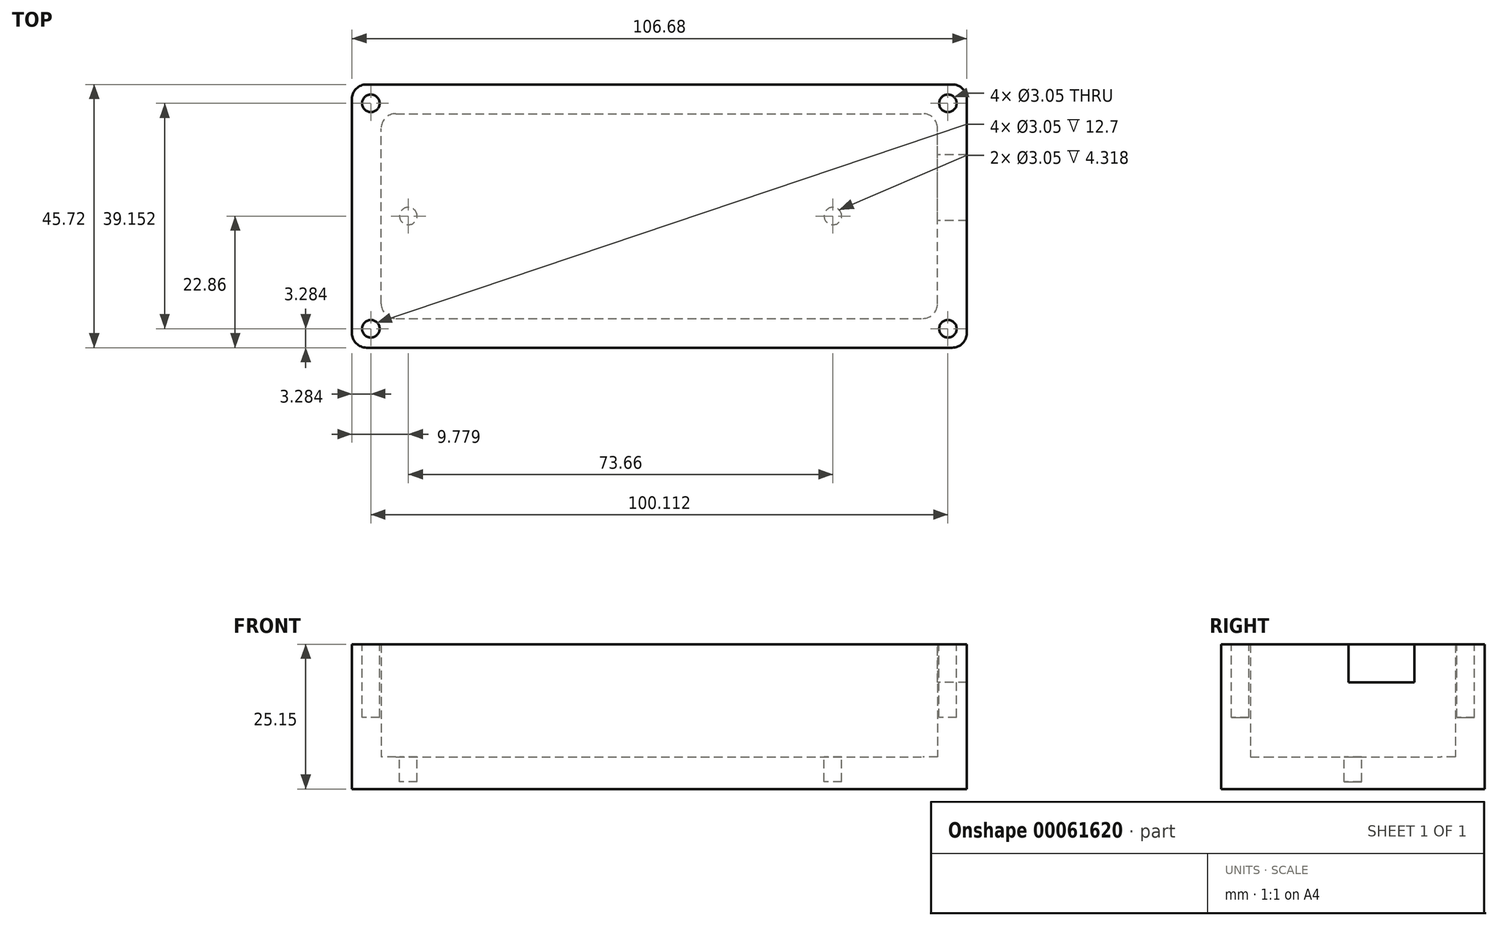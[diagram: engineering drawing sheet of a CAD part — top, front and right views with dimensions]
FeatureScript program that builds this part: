
annotation { "Feature Type Name" : "Feature", "Feature Type Description" : "" }
export const myFeature = defineFeature(function(context is Context, id is Id, definition is map)
    precondition{}
    {
        {
            var Q0;
            Q0=qCreatedBy(makeId("Top.planeOp"),FACE);
            var sketch = newSketch(context, id + "F0", { "sketchPlane" : qUnion([Q0])});
            skLineSegment(sketch, "E0.bottom", {"start": v(2.54, 0) * mm, "end": v(93.98, 0) * mm});
            skLineSegment(sketch, "E0.top", {"start": v(2.54, 35.56) * mm, "end": v(93.98, 35.56) * mm});
            skLineSegment(sketch, "E0.left", {"start": v(0, 2.54) * mm, "end": v(0, 33.02) * mm});
            skLineSegment(sketch, "E0.right", {"start": v(96.52, 2.54) * mm, "end": v(96.52, 33.02) * mm});
            skLineSegment(sketch, "E1.0", {"start": v(-2.54, 40.64) * mm, "end": v(99.06, 40.64) * mm});
            skLineSegment(sketch, "E1.1", {"start": v(-5.08, -2.54) * mm, "end": v(-5.08, 38.1) * mm});
            skLineSegment(sketch, "E1.2", {"start": v(-2.54, -5.08) * mm, "end": v(99.06, -5.08) * mm});
            skLineSegment(sketch, "E1.3", {"start": v(101.6, -2.54) * mm, "end": v(101.6, 38.1) * mm});
            skPoint(sketch, "E2.visualSharp", {"position": v(-5.08, -5.08) * mm});
            skArc(sketch, "E2.filletArc", {"start": v(-5.08, -2.54) * mm, "mid": v(-4.34, -4.34) * mm, "end": v(-2.54, -5.08) * mm});
            skPoint(sketch, "E3.visualSharp", {"position": v(101.6, 40.64) * mm});
            skArc(sketch, "E3.filletArc", {"start": v(101.6, 38.1) * mm, "mid": v(100.86, 39.9) * mm, "end": v(99.06, 40.64) * mm});
            skPoint(sketch, "E4.visualSharp", {"position": v(101.6, -5.08) * mm});
            skArc(sketch, "E4.filletArc", {"start": v(99.06, -5.08) * mm, "mid": v(100.86, -4.34) * mm, "end": v(101.6, -2.54) * mm});
            skPoint(sketch, "E5.visualSharp", {"position": v(-5.08, 40.64) * mm});
            skArc(sketch, "E5.filletArc", {"start": v(-2.54, 40.64) * mm, "mid": v(-4.34, 39.9) * mm, "end": v(-5.08, 38.1) * mm});
            skPoint(sketch, "E6.visualSharp", {"position": v(0, 0) * mm});
            skArc(sketch, "E6.filletArc", {"start": v(0, 2.54) * mm, "mid": v(0.74, 0.74) * mm, "end": v(2.54, 0) * mm});
            skPoint(sketch, "E7.visualSharp", {"position": v(0, 35.56) * mm});
            skArc(sketch, "E7.filletArc", {"start": v(2.54, 35.56) * mm, "mid": v(0.74, 34.82) * mm, "end": v(0, 33.02) * mm});
            skPoint(sketch, "E8.visualSharp", {"position": v(96.52, 35.56) * mm});
            skArc(sketch, "E8.filletArc", {"start": v(96.52, 33.02) * mm, "mid": v(95.78, 34.82) * mm, "end": v(93.98, 35.56) * mm});
            skPoint(sketch, "E9.visualSharp", {"position": v(96.52, 0) * mm});
            skArc(sketch, "E9.filletArc", {"start": v(93.98, 0) * mm, "mid": v(95.78, 0.74) * mm, "end": v(96.52, 2.54) * mm});
            skLineSegment(sketch, "E10.bottom", {"start": v(0.89, 1.27) * mm, "end": v(82.17, 1.27) * mm, "construction": true});
            skLineSegment(sketch, "E10.top", {"start": v(0.89, 34.3) * mm, "end": v(82.17, 34.3) * mm, "construction": true});
            skLineSegment(sketch, "E10.left", {"start": v(0.89, 1.27) * mm, "end": v(0.89, 34.3) * mm, "construction": true});
            skLineSegment(sketch, "E10.right", {"start": v(82.17, 1.27) * mm, "end": v(82.17, 34.3) * mm, "construction": true});
            skPoint(sketch, "E11", {"position": v(0, 17.78) * mm});
            skPoint(sketch, "E12", {"position": v(0.89, 17.78) * mm});
            skCircle(sketch, "E13", {"center": v(4.7, 17.78) * mm, "radius": 1.52 * mm});
            skCircle(sketch, "E14", {"center": v(78.36, 17.78) * mm, "radius": 1.52 * mm});
            skLineSegment(sketch, "E15", {"start": v(4.7, 17.78) * mm, "end": v(78.36, 17.78) * mm, "construction": true});
            skPoint(sketch, "E16", {"position": v(41.53, 17.78) * mm});
            skPoint(sketch, "E17", {"position": v(41.53, 34.3) * mm});
            skLineSegment(sketch, "E18.bottom", {"start": v(40.26, 31.12) * mm, "end": v(95.63, 31.12) * mm, "construction": true});
            skLineSegment(sketch, "E18.top", {"start": v(40.26, 4.44) * mm, "end": v(95.63, 4.44) * mm, "construction": true});
            skLineSegment(sketch, "E18.left", {"start": v(40.26, 31.12) * mm, "end": v(40.26, 4.44) * mm, "construction": true});
            skLineSegment(sketch, "E18.right", {"start": v(95.63, 31.12) * mm, "end": v(95.63, 4.44) * mm, "construction": true});
            skPoint(sketch, "E19", {"position": v(95.63, 17.78) * mm});
            skLineSegment(sketch, "E20", {"start": v(0, 17.78) * mm, "end": v(0.89, 17.78) * mm, "construction": true});
            skLineSegment(sketch, "E21", {"start": v(95.63, 17.78) * mm, "end": v(96.52, 17.78) * mm, "construction": true});
            skLineSegment(sketch, "E22.bottom", {"start": v(95.63, 27.3) * mm, "end": v(90.55, 27.3) * mm, "construction": true});
            skLineSegment(sketch, "E22.top", {"start": v(95.63, 18.16) * mm, "end": v(90.55, 18.16) * mm, "construction": true});
            skLineSegment(sketch, "E22.left", {"start": v(95.63, 27.3) * mm, "end": v(95.63, 18.16) * mm, "construction": true});
            skLineSegment(sketch, "E22.right", {"start": v(90.55, 27.3) * mm, "end": v(90.55, 18.16) * mm, "construction": true});
            skPoint(sketch, "E23", {"position": v(90.55, 22.73) * mm});
            skSolve(sketch);
        }
        {
            var Q0;
            Q0 = qSketchRegion(id + "F0", true);
            extrude(context, id + "F1", {"entities" : qUnion([Q0]), "depth" : 19.56 * mm});
        }
        {
            var Q0;
            Q0=makeQuery(id+"F0.imprint","IMPRINT",FACE,{"disambiguationData":[TD([[makeQuery(id+"F0.imprint","IMPRINT",EDGE,{"derivedFrom":sQuery(id+"F0.wireOp",EDGE,"E0.bottom")}),-1.0]])]});
            var Q1;
            Q1=makeQuery(id+"F0.imprint","IMPRINT",FACE,{"disambiguationData":[TD([[makeQuery(id+"F0.imprint","IMPRINT",EDGE,{"derivedFrom":sQuery(id+"F0.wireOp",EDGE,"E0.bottom")}),1.0]])]});
            var Q2;
            Q2=makeQuery(id+"F0.imprint","IMPRINT",FACE,{"disambiguationData":[TD([[makeQuery(id+"F0.imprint","IMPRINT",EDGE,{"derivedFrom":sQuery(id+"F0.wireOp",EDGE,"E14")}),1.0]])]});
            var Q3;
            Q3=makeQuery(id+"F0.imprint","IMPRINT",FACE,{"disambiguationData":[TD([[makeQuery(id+"F0.imprint","IMPRINT",EDGE,{"derivedFrom":sQuery(id+"F0.wireOp",EDGE,"E13")}),1.0]])]});
            extrude(context, id + "F2", {"entities" : qUnion([Q0, Q1, Q2, Q3]), "operationType" : NewBodyOperationType.ADD, "oppositeDirection" : true, "depth" : 5.6 * mm});
        }
        {
            var Q0;
            Q0=makeQuery(id+"F1.opExtrude","CAP_FACE",FACE,{"disambiguationData":[OSD([sQuery(id+"F0.wireOp",EDGE,"E0.bottom"),sQuery(id+"F0.wireOp",EDGE,"E0.top"),sQuery(id+"F0.wireOp",EDGE,"E0.left"),sQuery(id+"F0.wireOp",EDGE,"E0.right"),sQuery(id+"F0.wireOp",EDGE,"E1.0"),sQuery(id+"F0.wireOp",EDGE,"E1.1"),sQuery(id+"F0.wireOp",EDGE,"E1.2"),sQuery(id+"F0.wireOp",EDGE,"E1.3"),sQuery(id+"F0.wireOp",EDGE,"E2.filletArc"),sQuery(id+"F0.wireOp",EDGE,"E3.filletArc"),sQuery(id+"F0.wireOp",EDGE,"E4.filletArc"),sQuery(id+"F0.wireOp",EDGE,"E5.filletArc"),sQuery(id+"F0.wireOp",EDGE,"E6.filletArc"),sQuery(id+"F0.wireOp",EDGE,"E7.filletArc"),sQuery(id+"F0.wireOp",EDGE,"E8.filletArc"),sQuery(id+"F0.wireOp",EDGE,"E9.filletArc")])],"isStart":false});
            var sketch = newSketch(context, id + "F3", { "sketchPlane" : qUnion([Q0])});
            skLineSegment(sketch, "E24", {"start": v(0.74, 0.74) * mm, "end": v(-4.34, -4.34) * mm, "construction": true});
            skCircle(sketch, "E25", {"center": v(-1.8, -1.8) * mm, "radius": 1.52 * mm});
            skLineSegment(sketch, "E26", {"start": v(-4.34, 39.9) * mm, "end": v(0.74, 34.82) * mm, "construction": true});
            skLineSegment(sketch, "E27", {"start": v(95.78, 34.82) * mm, "end": v(100.86, 39.9) * mm, "construction": true});
            skLineSegment(sketch, "E28", {"start": v(95.78, 0.74) * mm, "end": v(100.86, -4.34) * mm, "construction": true});
            skCircle(sketch, "E29", {"center": v(-1.8, 37.36) * mm, "radius": 1.52 * mm});
            skCircle(sketch, "E30", {"center": v(98.32, 37.36) * mm, "radius": 1.52 * mm});
            skCircle(sketch, "E31", {"center": v(98.32, -1.8) * mm, "radius": 1.52 * mm});
            skSolve(sketch);
        }
        {
            var Q0;
            Q0 = qSketchRegion(id + "F3", true);
            extrude(context, id + "F4", {"entities" : qUnion([Q0]), "operationType" : NewBodyOperationType.REMOVE, "oppositeDirection" : true, "depth" : 12.7 * mm});
        }
        {
            var Q0;
            Q0=makeQuery(id+"F1.opExtrude","CAP_FACE",FACE,{"disambiguationData":[OSD([sQuery(id+"F0.wireOp",EDGE,"E0.bottom"),sQuery(id+"F0.wireOp",EDGE,"E0.top"),sQuery(id+"F0.wireOp",EDGE,"E0.left"),sQuery(id+"F0.wireOp",EDGE,"E0.right"),sQuery(id+"F0.wireOp",EDGE,"E1.0"),sQuery(id+"F0.wireOp",EDGE,"E1.1"),sQuery(id+"F0.wireOp",EDGE,"E1.2"),sQuery(id+"F0.wireOp",EDGE,"E1.3"),sQuery(id+"F0.wireOp",EDGE,"E2.filletArc"),sQuery(id+"F0.wireOp",EDGE,"E3.filletArc"),sQuery(id+"F0.wireOp",EDGE,"E4.filletArc"),sQuery(id+"F0.wireOp",EDGE,"E5.filletArc"),sQuery(id+"F0.wireOp",EDGE,"E6.filletArc"),sQuery(id+"F0.wireOp",EDGE,"E7.filletArc"),sQuery(id+"F0.wireOp",EDGE,"E8.filletArc"),sQuery(id+"F0.wireOp",EDGE,"E9.filletArc")])],"isStart":false});
            var sketch = newSketch(context, id + "F5", { "sketchPlane" : qUnion([Q0])});
            skLineSegment(sketch, "E32.bottom", {"start": v(101.6, 28.45) * mm, "end": v(96.52, 28.45) * mm});
            skLineSegment(sketch, "E32.top", {"start": v(101.6, 17.02) * mm, "end": v(96.52, 17.02) * mm});
            skLineSegment(sketch, "E32.left", {"start": v(101.6, 28.45) * mm, "end": v(101.6, 17.02) * mm});
            skLineSegment(sketch, "E32.right", {"start": v(96.52, 28.45) * mm, "end": v(96.52, 17.02) * mm});
            skPoint(sketch, "E33", {"position": v(96.52, 22.73) * mm});
            skSolve(sketch);
        }
        {
            var Q0;
            Q0 = qSketchRegion(id + "F5", true);
            extrude(context, id + "F6", {"entities" : qUnion([Q0]), "operationType" : NewBodyOperationType.REMOVE, "oppositeDirection" : true, "depth" : 6.6 * mm});
        }
        {
            var Q0;
            Q0=makeQuery(id+"F0.imprint","IMPRINT",FACE,{"disambiguationData":[TD([[makeQuery(id+"F0.imprint","IMPRINT",EDGE,{"derivedFrom":sQuery(id+"F0.wireOp",EDGE,"E13")}),1.0]])]});
            var Q1;
            Q1=makeQuery(id+"F0.imprint","IMPRINT",FACE,{"disambiguationData":[TD([[makeQuery(id+"F0.imprint","IMPRINT",EDGE,{"derivedFrom":sQuery(id+"F0.wireOp",EDGE,"E14")}),1.0]])]});
            extrude(context, id + "F7", {"entities" : qUnion([Q0, Q1]), "operationType" : NewBodyOperationType.REMOVE, "oppositeDirection" : true, "depth" : 4.32 * mm});
        }
        {
            var Q0;
            Q0=makeQuery(id+"F1.opExtrude","CAP_FACE",FACE,{"disambiguationData":[OSD([sQuery(id+"F0.wireOp",EDGE,"E0.bottom"),sQuery(id+"F0.wireOp",EDGE,"E0.top"),sQuery(id+"F0.wireOp",EDGE,"E0.left"),sQuery(id+"F0.wireOp",EDGE,"E0.right"),sQuery(id+"F0.wireOp",EDGE,"E1.0"),sQuery(id+"F0.wireOp",EDGE,"E1.1"),sQuery(id+"F0.wireOp",EDGE,"E1.2"),sQuery(id+"F0.wireOp",EDGE,"E1.3"),sQuery(id+"F0.wireOp",EDGE,"E2.filletArc"),sQuery(id+"F0.wireOp",EDGE,"E3.filletArc"),sQuery(id+"F0.wireOp",EDGE,"E4.filletArc"),sQuery(id+"F0.wireOp",EDGE,"E5.filletArc"),sQuery(id+"F0.wireOp",EDGE,"E6.filletArc"),sQuery(id+"F0.wireOp",EDGE,"E7.filletArc"),sQuery(id+"F0.wireOp",EDGE,"E8.filletArc"),sQuery(id+"F0.wireOp",EDGE,"E9.filletArc")])],"isStart":false});
            var sketch = newSketch(context, id + "F8", { "sketchPlane" : qUnion([Q0])});
            skLineSegment(sketch, "E34.0", {"start": v(-2.54, 40.64) * mm, "end": v(99.06, 40.64) * mm});
            skArc(sketch, "E35.0", {"start": v(101.6, 38.1) * mm, "mid": v(100.86, 39.9) * mm, "end": v(99.06, 40.64) * mm});
            skArc(sketch, "E35.2", {"start": v(99.06, -5.08) * mm, "mid": v(100.86, -4.34) * mm, "end": v(101.6, -2.54) * mm});
            skLineSegment(sketch, "E35.3", {"start": v(-2.54, -5.08) * mm, "end": v(99.06, -5.08) * mm});
            skArc(sketch, "E35.4", {"start": v(-5.08, -2.54) * mm, "mid": v(-4.34, -4.34) * mm, "end": v(-2.54, -5.08) * mm});
            skLineSegment(sketch, "E35.5", {"start": v(-5.08, -2.54) * mm, "end": v(-5.08, 38.1) * mm});
            skArc(sketch, "E35.6", {"start": v(-2.54, 40.64) * mm, "mid": v(-4.34, 39.9) * mm, "end": v(-5.08, 38.1) * mm});
            skLineSegment(sketch, "E36.0", {"start": v(101.6, -2.54) * mm, "end": v(101.6, 38.1) * mm});
            skCircle(sketch, "E37.0", {"center": v(98.32, 37.36) * mm, "radius": 1.52 * mm});
            skCircle(sketch, "E37.1", {"center": v(98.32, -1.8) * mm, "radius": 1.52 * mm});
            skCircle(sketch, "E37.2", {"center": v(-1.8, -1.8) * mm, "radius": 1.52 * mm});
            skCircle(sketch, "E37.3", {"center": v(-1.8, 37.36) * mm, "radius": 1.52 * mm});
            skSolve(sketch);
        }
        {
            var Q0;
            Q0 = qSketchRegion(id + "F8", true);
            extrude(context, id + "F9", {"entities" : qUnion([Q0]), "depth" : 1 / 406.4 * mm});
        }
    });
